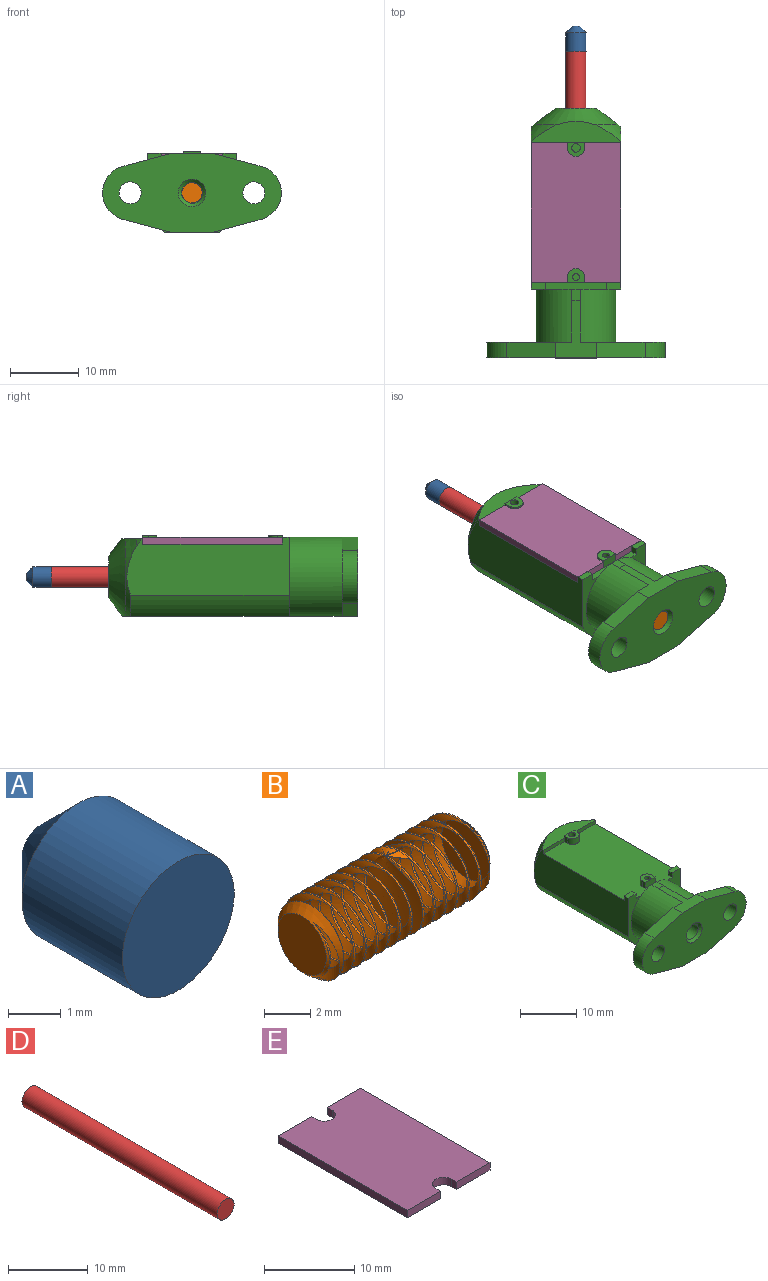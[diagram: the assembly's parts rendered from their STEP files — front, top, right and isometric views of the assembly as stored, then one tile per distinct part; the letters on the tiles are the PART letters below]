
ASSEMBLY  parts=5 mates=4
PART A: 4 faces, bbox 3x3.7x3 mm
  f0: cone r=1mm half-angle=45deg, axis (0,-1,0), area 8.9mm2, adj f1,f2
  f1: cylinder r=1.5mm len=3mm, axis (0,1,0), area 25.4mm2, adj f0,f3
  f2: plane 1x1mm, normal (0,1,0), area 0.8mm2, adj f0
  f3: plane 3x3mm, normal (0,-1,0), area 7.1mm2, adj f1
PART B: 8 faces, bbox 10.4x4.1x4.1 mm
  f0: cylinder r=2mm len=8.95mm, axis (1,0,0), area 15.7mm2, adj f1,f2,f5,f7
  f1: cone r=1.47mm half-angle=45deg, axis (-1,0,0), area 4.4mm2, adj f0,f4,f5,f6,f7
  f2: cone r=2mm half-angle=45deg, axis (1,0,0), area 4.4mm2, adj f0,f3,f5,f6,f7
  f3: plane 2.95x2.95mm, normal (-1,0,0), area 6.8mm2, adj f2
  f4: plane 2.95x2.95mm, normal (1,0,0), area 6.8mm2, adj f1
  f5: bspline ~10.14x4.08mm, area 56.7mm2, adj f0,f1,f2,f6
  f6: cylinder r=1.55mm len=9.86mm, axis (1,0,0), area 14.3mm2, adj f1,f2,f5,f7
  f7: bspline ~10.28x4.07mm, area 44.5mm2, adj f0,f1,f2,f6
PART C: 56 faces, bbox 26x36.3x14.3 mm
  f0: cone r=1.75mm half-angle=45deg, axis (0,-1,0), area 7.8mm2, adj f1,f2
  f1: plane 26x11.53mm, normal (0,-1,0), area 209.9mm2, adj f0,f7,f12,f13,f14,f15,f16,f17
  f2: cylinder r=1.5mm len=35.8mm, axis (0,1,0), area 337.4mm2, adj f0,f55
  f3: plane 2.5x2mm, normal (0,0,1), area 3.5mm2, adj f25,f37,f38,f39,f45
  f4: plane 2.5x2mm, normal (0,0,1), area 3.1mm2, adj f23,f27,f34,f35,f36
  f5: plane 1.29x0mm, normal (0,1,0), area 0mm2, adj f6,f7,f8,f9
  f6: plane 1.7x1.29mm, normal (0,0,1), area 2.2mm2, adj f5,f8,f9,f10
  f7: plane 8.3x6mm, normal (0,0,1), area 21.4mm2, adj f1,f5,f8,f9,f11,f14,f19,f20
  f8: cylinder r=5.8mm len=11.53mm, axis (0,1,0), area 130.5mm2, adj f5,f6,f7,f10,f11,f22,f53
  f9: cylinder r=5.8mm len=11.53mm, axis (0,1,0), area 130.5mm2, adj f5,f6,f7,f10,f20,f21,f53
  f10: plane 6.62x1mm, normal (0,1,0), area 4.6mm2, adj f6,f8,f9,f47
  f11: plane 12.36x11.53mm, normal (0,1,0), area 58.4mm2, adj f7,f8,f13,f14,f15,f16,f53
  f12: cylinder r=1.6mm len=3.2mm, axis (0,1,0), area 23.1mm2, adj f1,f20
  f13: cylinder r=1.6mm len=3.2mm, axis (0,1,0), area 23.1mm2, adj f1,f11
  f14: plane 7.04x2.3mm, normal (-0.26,0,0.97), area 16.8mm2, adj f1,f7,f11,f15
  f15: cylinder r=4mm len=7.72mm, axis (0,1,0), area 24mm2, adj f1,f11,f14,f16
  f16: plane 7.04x2.3mm, normal (-0.26,0,-0.97), area 16.8mm2, adj f1,f11,f15,f53
  f17: plane 7.04x2.3mm, normal (0.26,0,-0.97), area 16.8mm2, adj f1,f18,f20,f53
  f18: cylinder r=4mm len=7.72mm, axis (0,1,0), area 24mm2, adj f1,f17,f19,f20
  f19: plane 7.04x2.3mm, normal (0.26,0,0.97), area 16.8mm2, adj f1,f7,f18,f20
  f20: plane 12.36x11.53mm, normal (0,1,0), area 58.4mm2, adj f7,f9,f12,f17,f18,f19,f53
  f21: plane 11.53x5.86mm, normal (0,-1,0), area 16.8mm2, adj f9,f41,f42,f44,f47,f49,f53
  f22: plane 11.53x5.86mm, normal (0,-1,0), area 16.8mm2, adj f8,f30,f43,f46,f47,f52,f53
  f23: cylinder r=0.62mm len=2.25mm, axis (0,0,-1), area 8.8mm2, adj f4,f24
  f24: plane 1.25x1.25mm, normal (0,0,1), area 1.2mm2, adj f23
  f25: cylinder r=0.5mm len=2.25mm, axis (0,0,-1), area 7.1mm2, adj f3,f26
  f26: plane 1x1mm, normal (0,0,1), area 0.8mm2, adj f25
  f27: plane 2.5x0.5mm, normal (0,1,0), area 1.3mm2, adj f4,f28,f34,f36
  f28: plane 13x3.36mm, normal (0,0,1), area 28.1mm2, adj f27,f29,f30,f31,f33,f41,f48,f50
  f29: plane 5.25x0.75mm, normal (0,-1,0), area 3.9mm2, adj f28,f30,f36,f47
  f30: plane 24.02x8.41mm, normal (-1,0,0), area 173.3mm2, adj f22,f28,f29,f31,f32,f43,f47,f51
  f31: cone r=7.85mm half-angle=39.9deg, axis (0,-1,0), area 0.6mm2, adj f28,f30,f51
  f32: plane 2x1mm, normal (0,1,0), area 2mm2, adj f30,f43,f46,f47
  f33: plane 5.25x0.75mm, normal (0,-1,0), area 3.9mm2, adj f28,f34,f41,f47
  f34: plane 1.25x0.75mm, normal (1,0,0), area 0.9mm2, adj f4,f27,f33,f35,f47
  f35: cylinder r=1.25mm len=2.5mm, axis (0,0,-1), area 4.9mm2, adj f4,f34,f36,f47
  f36: plane 1.25x0.75mm, normal (-1,0,0), area 0.9mm2, adj f4,f27,f29,f35,f47
  f37: plane 1.25x0.75mm, normal (-1,0,0), area 0.9mm2, adj f3,f38,f45,f47
  f38: cylinder r=1.25mm len=2.5mm, axis (0,0,-1), area 4.9mm2, adj f3,f37,f39,f47
  f39: plane 1.25x0.75mm, normal (1,0,0), area 0.9mm2, adj f3,f38,f45,f47
  f40: plane 2x1mm, normal (0,1,0), area 2mm2, adj f41,f42,f44,f47
  f41: plane 24.02x8.41mm, normal (1,0,0), area 173.3mm2, adj f21,f28,f33,f40,f42,f47,f48,f49
  f42: plane 2x1mm, normal (0,0,1), area 2mm2, adj f21,f40,f41,f44
  f43: plane 2x1mm, normal (0,0,1), area 2mm2, adj f22,f30,f32,f46
  f44: plane 1x1mm, normal (-1,0,0), area 1mm2, adj f21,f40,f42,f47
  f45: plane 2.5x1.25mm, normal (0,-1,0), area 3.1mm2, adj f3,f37,f39,f47
  f46: plane 1x1mm, normal (1,0,0), area 1mm2, adj f22,f32,f43,f47
  f47: plane 21.3x13mm, normal (0,0,1), area 264.2mm2, adj f10,f21,f22,f29,f30,f32,f33,f34
  f48: cone r=7.06mm half-angle=45.4deg, axis (0,-1,0), area 15.4mm2, adj f28,f41,f49,f50,f53,f54
  f49: cylinder r=7.02mm len=23.11mm, axis (0,1,0), area 93.7mm2, adj f21,f41,f48,f53
  f50: cone r=7.85mm half-angle=39.9deg, axis (0,-1,0), area 0.6mm2, adj f28,f41,f48
  f51: cone r=7.06mm half-angle=45.4deg, axis (0,-1,0), area 15.4mm2, adj f28,f30,f31,f52,f53,f54
  f52: cylinder r=7.02mm len=23.11mm, axis (0,1,0), area 93.7mm2, adj f22,f30,f51,f53
  f53: plane 34.38x8mm, normal (0,0,-1), area 214.6mm2, adj f1,f8,f9,f11,f16,f17,f20,f21
  f54: cone r=5.02mm half-angle=53.1deg, axis (0,-1,0), area 111.3mm2, adj f28,f48,f51,f53,f55
  f55: plane 6.03x6.03mm, normal (0,1,0), area 21.5mm2, adj f2,f54
PART D: 3 faces, bbox 3x34.6x3 mm
  f0: plane 3x3mm, normal (0,-1,0), area 7.1mm2, adj f2
  f1: plane 3x3mm, normal (0,1,0), area 7.1mm2, adj f2
  f2: cylinder r=1.5mm len=34.6mm, axis (0,1,0), area 326.1mm2, adj f0,f1
PART E: 14 faces, bbox 13x20.3x1 mm
  f0: plane 20.3x13mm, normal (0,0,1), area 255.2mm2, adj f2,f3,f4,f5,f6,f7,f8,f9
  f1: plane 20.3x13mm, normal (0,0,-1), area 255.2mm2, adj f2,f3,f4,f5,f6,f7,f8,f9
  f2: plane 1x0.75mm, normal (-1,0,0), area 0.8mm2, adj f0,f1,f3,f13
  f3: cylinder r=1.25mm len=2.5mm, axis (0,0,1), area 3.9mm2, adj f0,f1,f2,f4
  f4: plane 1x0.75mm, normal (1,0,0), area 0.8mm2, adj f0,f1,f3,f5
  f5: plane 5.25x1mm, normal (0,-1,0), area 5.2mm2, adj f0,f1,f4,f6
  f6: plane 20.3x1mm, normal (-1,0,0), area 20.3mm2, adj f0,f1,f5,f7
  f7: plane 5.25x1mm, normal (0,1,0), area 5.2mm2, adj f0,f1,f6,f8
  f8: plane 1x0.75mm, normal (1,0,0), area 0.8mm2, adj f0,f1,f7,f9
  f9: cylinder r=1.25mm len=2.5mm, axis (0,0,1), area 3.9mm2, adj f0,f1,f8,f10
  f10: plane 1x0.75mm, normal (-1,0,0), area 0.8mm2, adj f0,f1,f9,f11
  f11: plane 5.25x1mm, normal (0,1,0), area 5.2mm2, adj f0,f1,f10,f12
  f12: plane 20.3x1mm, normal (1,0,0), area 20.3mm2, adj f0,f1,f11,f13
  f13: plane 5.25x1mm, normal (0,-1,0), area 5.2mm2, adj f0,f1,f2,f12
PLACE A t=(-24.68,-10.03,6.91)mm
PLACE B rot(axis=(0.58,0.58,0.58),120deg) t=(-15.68,-4.53,6.91)mm
PLACE C t=(-24.68,-10.03,6.91)mm
PLACE D t=(-24.68,-10.03,6.91)mm
PLACE E t=(-24.68,-10.03,6.91)mm
MATE fastened B.f0 <-> C.f51  axis (0,-1,0) through (-15.68,-9.53,6.91)mm
MATE fastened A.f0 <-> D.f2  axis (0,-1,0) through (-15.68,34.57,6.91)mm
MATE fastened E.f9 <-> C.f23  axis (0,0,-1) through (-15.68,20.52,11.68)mm
MATE fastened A.f0 <-> C.f0  axis (0,-1,0) through (-15.68,38.27,6.91)mm
